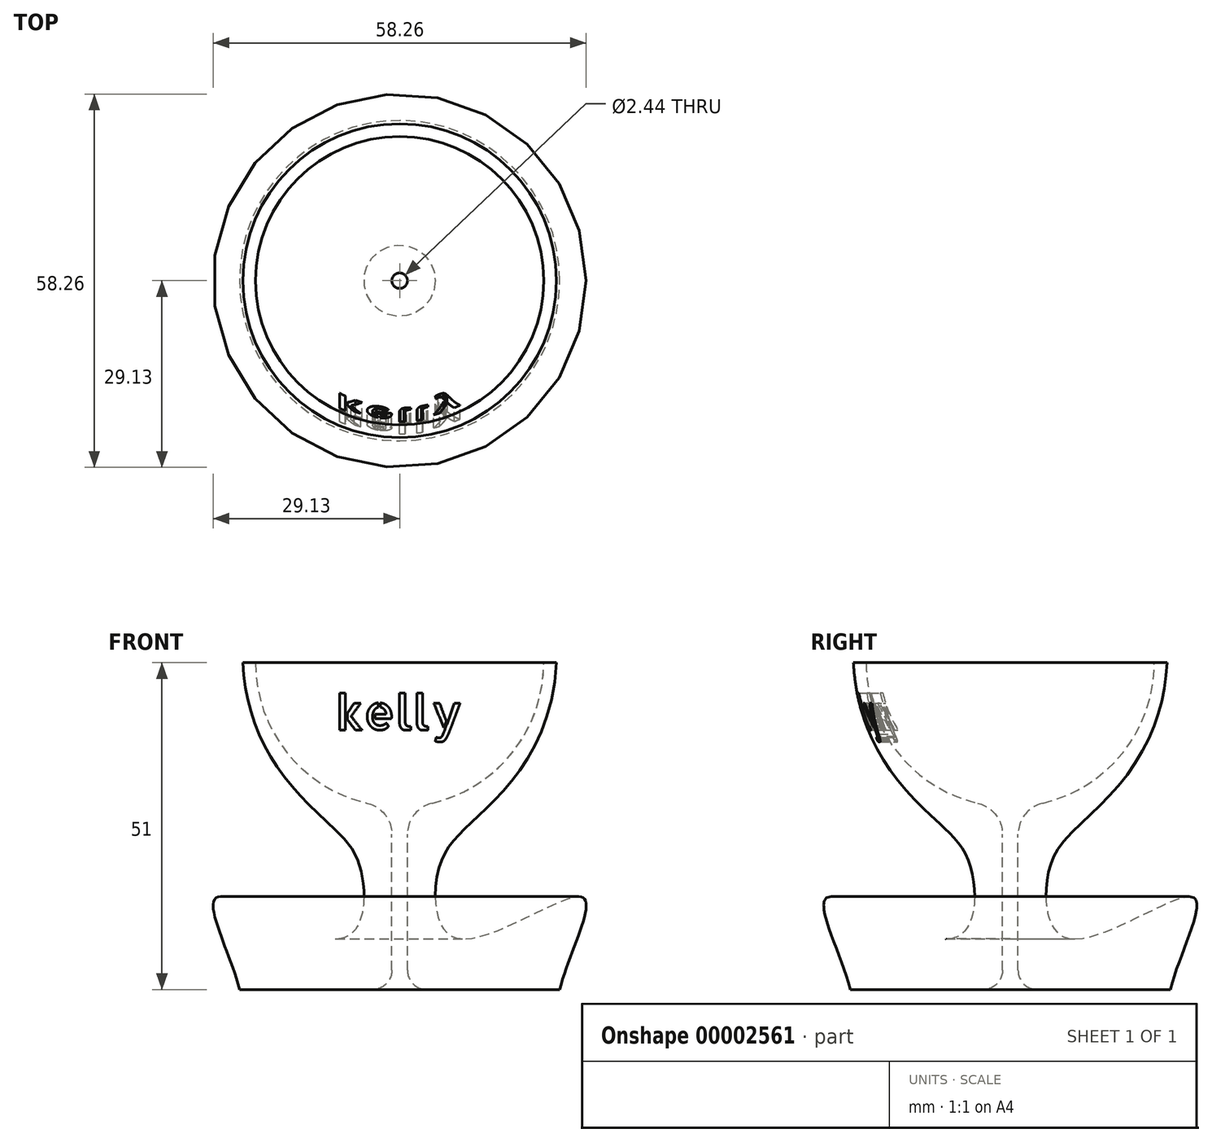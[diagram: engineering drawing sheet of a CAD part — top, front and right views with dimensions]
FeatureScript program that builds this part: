
annotation { "Feature Type Name" : "Feature", "Feature Type Description" : "" }
export const myFeature = defineFeature(function(context is Context, id is Id, definition is map)
    precondition{}
    {
        {
            var Q0;
            Q0=qCreatedBy(makeId("Front.planeOp"),FACE);
            var sketch = newSketch(context, id + "F0", { "sketchPlane" : qUnion([Q0])});
            skCircle(sketch, "E0", {"center": v(0, 0) * mm, "radius": 22.5 * mm});
            skLineSegment(sketch, "E1", {"start": v(0, 0) * mm, "end": v(0, -51) * mm});
            skLineSegment(sketch, "E2", {"start": v(0, -51) * mm, "end": v(-25, -51) * mm});
            skLineSegment(sketch, "E3", {"start": v(0, 0) * mm, "end": v(-24.5, 0) * mm});
            skFitSpline(sketch, "E4", {"points": [v(-24.5, 0) * mm, v(-11.07, -25.07) * mm, v(-5.93, -32.88) * mm, v(-9.14, -43.03) * mm, v(-28.52, -36.6) * mm, v(-25, -51) * mm], "startDerivative": vector(8.56, -154.25) * mm, "endDerivative": vector(21.18, -86.7) * mm});
            skLineSegment(sketch, "E5", {"start": v(-1.22, -51) * mm, "end": v(-1.22, -22.47) * mm});
            skSolve(sketch);
        }
        {
            var Q0;
            {var subQ0=sQuery(id+"F0.wireOp",EDGE,"E4");Q0=makeQuery(id+"F0.imprint","IMPRINT",FACE,{"disambiguationData":[TD([[makeQuery(id+"F0.imprint","IMPRINT",EDGE,{"derivedFrom":subQ0}),1.0]])]});}
            var Q1;
            Q1=sQuery(id+"F0.wireOp",EDGE,"E1");
            revolve(context, id + "F1", {"entities" : qUnion([Q0]), "axis" : qUnion([Q1]), "revolveType" : RevolveType.FULL});
        }
        {
            var Q0;
            Q0=qCreatedBy(makeId("Front.planeOp"),FACE);
            var sketch = newSketch(context, id + "F2", { "sketchPlane" : qUnion([Q0])});
            skText(sketch, "E6", { "text": "kelly", "fontName": "AllertaStencil-Regular.ttf"});
            skLineSegment(sketch, "E7", {"start": v(0, -5) * mm, "end": v(0, 0) * mm, "construction": true});
            const initialGuessF2  = {"E6": [-0.01, -0.0105, 1, 0, 0.0055]};
            skSetInitialGuess(sketch, initialGuessF2);
            skSolve(sketch);
        }
        {
            var Q0;
            Q0 = qSketchRegion(id + "F2", true);
            extrude(context, id + "F3", {"entities" : qUnion([Q0]), "operationType" : NewBodyOperationType.REMOVE, "depth" : 27.6 * mm});
        }
        {
            var Q0;
            Q0=makeQuery(id+"F1.opRevolve","SWEPT_EDGE",EDGE,{"disambiguationData":[OSD([sQuery(id+"F0.wireOp",EDGE,"E0"),sQuery(id+"F0.wireOp",EDGE,"E5")])]});
            fillet(context, id + "F4", {"entities" : qUnion([Q0]), "radius" : 5 * mm, "tangentPropagation" : true, "allowEdgeOverflow" : false});
        }
        {
            var Q0;
            Q0=makeQuery(id+"F1.opRevolve","SWEPT_EDGE",EDGE,{"disambiguationData":[OSD([sQuery(id+"F0.wireOp",EDGE,"E2"),sQuery(id+"F0.wireOp",EDGE,"E5")])]});
            fillet(context, id + "F5", {"entities" : qUnion([Q0]), "radius" : 3 * mm, "tangentPropagation" : true, "allowEdgeOverflow" : false});
        }
    });
